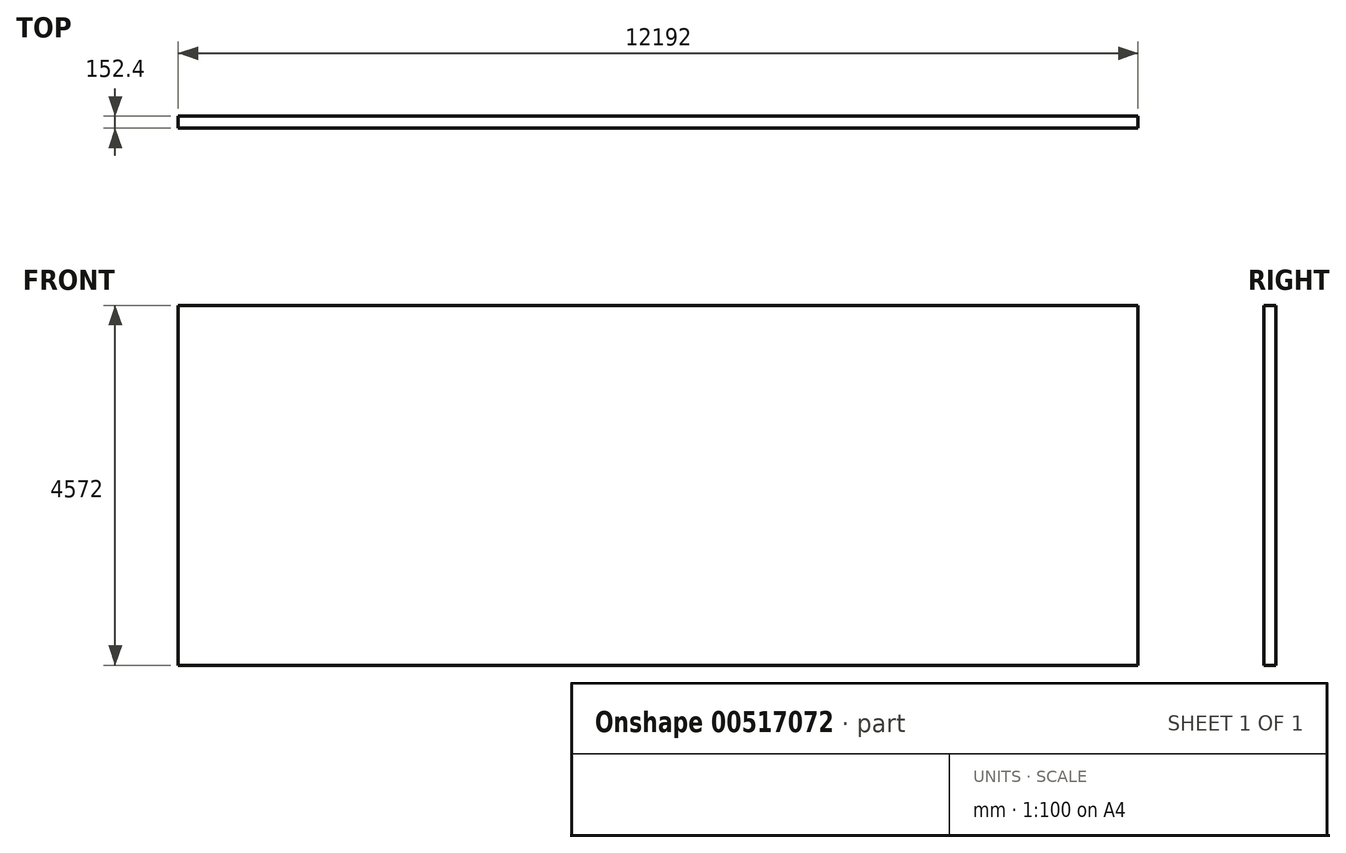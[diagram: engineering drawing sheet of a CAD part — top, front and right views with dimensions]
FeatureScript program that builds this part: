
annotation { "Feature Type Name" : "Feature", "Feature Type Description" : "" }
export const myFeature = defineFeature(function(context is Context, id is Id, definition is map)
    precondition{}
    {
        {
            var Q0;
            Q0=qCreatedBy(makeId("Front.planeOp"),FACE);
            var sketch = newSketch(context, id + "F0", { "sketchPlane" : qUnion([Q0])});
            skLineSegment(sketch, "E0.bottom", {"start": v(-5146.62, 1603.76) * mm, "end": v(7045.38, 1603.76) * mm});
            skLineSegment(sketch, "E0.top", {"start": v(-5146.62, -2968.24) * mm, "end": v(7045.38, -2968.24) * mm});
            skLineSegment(sketch, "E0.left", {"start": v(-5146.62, 1603.76) * mm, "end": v(-5146.62, -2968.24) * mm});
            skLineSegment(sketch, "E0.right", {"start": v(7045.38, 1603.76) * mm, "end": v(7045.38, -2968.24) * mm});
            skSolve(sketch);
        }
        {
            var Q0;
            Q0=makeQuery(id+"F0.imprint","IMPRINT",FACE,{"disambiguationData":[TD([[makeQuery(id+"F0.imprint","IMPRINT",EDGE,{"derivedFrom":sQuery(id+"F0.wireOp",EDGE,"E0.bottom")}),-1.0]])]});
            extrude(context, id + "F1", {"entities" : qUnion([Q0]), "depth" : 152.4 * mm, "offsetDistance" : 30.48 * mm});
        }
    });
